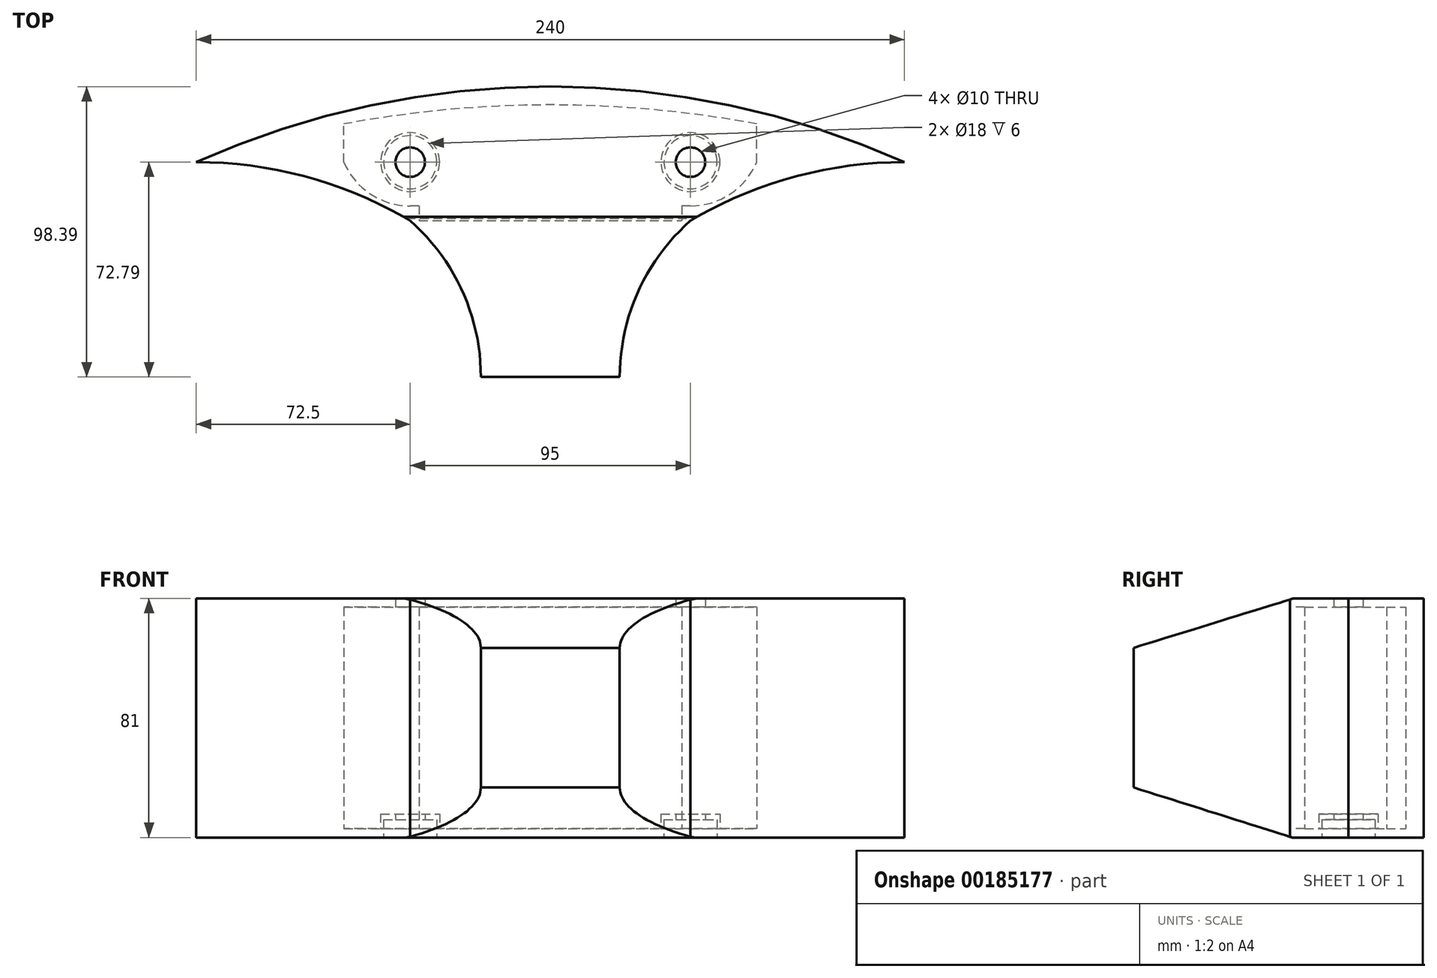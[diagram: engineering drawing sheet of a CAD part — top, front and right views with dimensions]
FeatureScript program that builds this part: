
annotation { "Feature Type Name" : "Feature", "Feature Type Description" : "" }
export const myFeature = defineFeature(function(context is Context, id is Id, definition is map)
    precondition{}
    {
        {
            var Q0;
            Q0=qCreatedBy(makeId("Top.planeOp"),FACE);
            var sketch = newSketch(context, id + "F0", { "sketchPlane" : qUnion([Q0])});
            skLineSegment(sketch, "E0.bottom", {"start": v(47.5, 12.5) * mm, "end": v(-47.5, 12.5) * mm, "construction": true});
            skLineSegment(sketch, "E0.top", {"start": v(47.5, -12.5) * mm, "end": v(-47.5, -12.5) * mm, "construction": true});
            skLineSegment(sketch, "E0.left", {"start": v(47.5, 12.5) * mm, "end": v(47.5, -12.5) * mm, "construction": true});
            skLineSegment(sketch, "E0.right", {"start": v(-47.5, 12.5) * mm, "end": v(-47.5, -12.5) * mm, "construction": true});
            skPoint(sketch, "E0.middle", {"position": v(0, 0) * mm});
            skCircle(sketch, "E1", {"center": v(-47.5, 0) * mm, "radius": 12.5 * mm, "construction": true});
            skCircle(sketch, "E2", {"center": v(47.5, 0) * mm, "radius": 12.5 * mm, "construction": true});
            skLineSegment(sketch, "E3", {"start": v(0, 12.5) * mm, "end": v(0, -72.5) * mm, "construction": true});
            skPoint(sketch, "E3.endSnap0", {"position": v(0, 12.5) * mm});
            skLineSegment(sketch, "E4.bottom", {"start": v(-23.5, -72.5) * mm, "end": v(23.5, -72.5) * mm, "construction": true});
            skLineSegment(sketch, "E4.top", {"start": v(-23.5, -72.5) * mm, "end": v(23.5, -72.5) * mm, "construction": true});
            skLineSegment(sketch, "E4.left", {"start": v(-23.5, -72.5) * mm, "end": v(-23.5, -72.5) * mm});
            skLineSegment(sketch, "E4.right", {"start": v(23.5, -72.5) * mm, "end": v(23.5, -72.5) * mm});
            skPoint(sketch, "E4.middle", {"position": v(0, -72.5) * mm});
            skLineSegment(sketch, "E5.bottom", {"start": v(47.5, -19.83) * mm, "end": v(-47.5, -19.83) * mm});
            skLineSegment(sketch, "E5.top", {"start": v(47.5, -14.83) * mm, "end": v(-47.5, -14.83) * mm});
            skLineSegment(sketch, "E5.left", {"start": v(47.5, -19.83) * mm, "end": v(47.5, -14.83) * mm});
            skLineSegment(sketch, "E5.right", {"start": v(-47.5, -19.83) * mm, "end": v(-47.5, -14.83) * mm});
            skPoint(sketch, "E5.middle", {"position": v(0, -17.33) * mm});
            skLineSegment(sketch, "E6.bottom", {"start": v(120, 0) * mm, "end": v(-120, 0) * mm, "construction": true});
            skLineSegment(sketch, "E6.top", {"start": v(120, 0) * mm, "end": v(-120, 0) * mm, "construction": true});
            skLineSegment(sketch, "E6.left", {"start": v(120, 0) * mm, "end": v(120, 0) * mm});
            skLineSegment(sketch, "E6.right", {"start": v(-120, 0) * mm, "end": v(-120, 0) * mm});
            skArc(sketch, "E7", {"start": v(-47.5, -19.83) * mm, "mid": v(-82.42, -5.05) * mm, "end": v(-120, 0) * mm});
            skArc(sketch, "E8", {"start": v(120, 0) * mm, "mid": v(82.42, -5.05) * mm, "end": v(47.5, -19.83) * mm});
            skArc(sketch, "E9", {"start": v(120, 0) * mm, "mid": v(0, 25.6) * mm, "end": v(-120, 0) * mm});
            skArc(sketch, "E10", {"start": v(-70, 0) * mm, "mid": v(-60.97, -10.79) * mm, "end": v(-47.5, -14.83) * mm});
            skArc(sketch, "E11", {"start": v(47.5, -14.83) * mm, "mid": v(60.97, -10.79) * mm, "end": v(70, 0) * mm});
            skArc(sketch, "E12", {"start": v(70, 12.91) * mm, "mid": v(0, 19.4) * mm, "end": v(-70, 12.91) * mm});
            skLineSegment(sketch, "E13", {"start": v(-70, 0) * mm, "end": v(-70, 12.91) * mm});
            skLineSegment(sketch, "E14", {"start": v(70, 0) * mm, "end": v(70, 12.91) * mm});
            skSolve(sketch);
        }
        {
            var Q0;
            Q0=qSketchRegion(id+"F0",true);
            extrude(context, id + "F1", {"entities" : qUnion([Q0]), "depth" : 75 * mm});
        }
        {
            var Q0;
            Q0=makeQuery(id+"F1.opExtrude","CAP_FACE",FACE,{"disambiguationData":[OSD([sQuery(id+"F0.wireOp",EDGE,"E5.bottom"),sQuery(id+"F0.wireOp",EDGE,"E5.top"),sQuery(id+"F0.wireOp",EDGE,"E7"),sQuery(id+"F0.wireOp",EDGE,"E8"),sQuery(id+"F0.wireOp",EDGE,"E9"),sQuery(id+"F0.wireOp",EDGE,"E10"),sQuery(id+"F0.wireOp",EDGE,"E11"),sQuery(id+"F0.wireOp",EDGE,"E12"),sQuery(id+"F0.wireOp",EDGE,"E13"),sQuery(id+"F0.wireOp",EDGE,"E14")])],"isStart":true});
            var sketch = newSketch(context, id + "F2", { "sketchPlane" : qUnion([Q0])});
            skArc(sketch, "E15", {"start": v(-120, 0) * mm, "mid": v(-82.42, 5.05) * mm, "end": v(-47.5, 19.83) * mm});
            skArc(sketch, "E16", {"start": v(47.5, 19.83) * mm, "mid": v(82.42, 5.05) * mm, "end": v(120, 0) * mm});
            skArc(sketch, "E17", {"start": v(-120, 0) * mm, "mid": v(0, -25.6) * mm, "end": v(120, 0) * mm});
            skLineSegment(sketch, "E18", {"start": v(-47.5, 19.83) * mm, "end": v(47.5, 19.83) * mm});
            skSolve(sketch);
        }
        {
            var Q0;
            Q0=qSketchRegion(id+"F2",true);
            extrude(context, id + "F3", {"entities" : qUnion([Q0]), "operationType" : NewBodyOperationType.ADD, "depth" : 3 * mm});
        }
        {
            var Q0;
            Q0=makeQuery(id+"F3.opExtrude","CAP_FACE",FACE,{"disambiguationData":[OSD([sQuery(id+"F2.wireOp",EDGE,"E15"),sQuery(id+"F2.wireOp",EDGE,"E16"),sQuery(id+"F2.wireOp",EDGE,"E17"),sQuery(id+"F2.wireOp",EDGE,"E18")])],"isStart":false});
            var sketch = newSketch(context, id + "F4", { "sketchPlane" : qUnion([Q0])});
            skLineSegment(sketch, "E19.bottom", {"start": v(47.5, 12.5) * mm, "end": v(-47.5, 12.5) * mm, "construction": true});
            skLineSegment(sketch, "E19.top", {"start": v(47.5, -12.5) * mm, "end": v(-47.5, -12.5) * mm, "construction": true});
            skLineSegment(sketch, "E19.left", {"start": v(47.5, 12.5) * mm, "end": v(47.5, -12.5) * mm, "construction": true});
            skLineSegment(sketch, "E19.right", {"start": v(-47.5, 12.5) * mm, "end": v(-47.5, -12.5) * mm, "construction": true});
            skPoint(sketch, "E19.middle", {"position": v(0, 0) * mm});
            skCircle(sketch, "E20", {"center": v(-47.5, 0) * mm, "radius": 10 * mm});
            skCircle(sketch, "E21", {"center": v(47.5, 0) * mm, "radius": 10 * mm});
            skSolve(sketch);
        }
        {
            var Q0;
            Q0=qSketchRegion(id+"F4",true);
            extrude(context, id + "F5", {"entities" : qUnion([Q0]), "operationType" : NewBodyOperationType.ADD, "oppositeDirection" : true, "depth" : 8 * mm});
        }
        {
            var Q0;
            Q0=makeQuery(id+"F3.opExtrude","CAP_FACE",FACE,{"disambiguationData":[OSD([sQuery(id+"F2.wireOp",EDGE,"E15"),sQuery(id+"F2.wireOp",EDGE,"E16"),sQuery(id+"F2.wireOp",EDGE,"E17"),sQuery(id+"F2.wireOp",EDGE,"E18")])],"isStart":false});
            var sketch = newSketch(context, id + "F6", { "sketchPlane" : qUnion([Q0])});
            skCircle(sketch, "E22", {"center": v(-47.5, 0) * mm, "radius": 9 * mm});
            skCircle(sketch, "E23", {"center": v(47.5, 0) * mm, "radius": 9 * mm});
            skSolve(sketch);
        }
        {
            var Q0;
            Q0=qSketchRegion(id+"F6",true);
            extrude(context, id + "F7", {"entities" : qUnion([Q0]), "operationType" : NewBodyOperationType.REMOVE, "oppositeDirection" : true, "depth" : 6 * mm});
        }
        {
            var Q0;
            Q0=makeQuery(id+"F3.opExtrude","CAP_FACE",FACE,{"disambiguationData":[OSD([sQuery(id+"F2.wireOp",EDGE,"E15"),sQuery(id+"F2.wireOp",EDGE,"E16"),sQuery(id+"F2.wireOp",EDGE,"E17"),sQuery(id+"F2.wireOp",EDGE,"E18")])],"isStart":false});
            var sketch = newSketch(context, id + "F8", { "sketchPlane" : qUnion([Q0])});
            skCircle(sketch, "E24", {"center": v(-47.5, 0) * mm, "radius": 5 * mm});
            skCircle(sketch, "E25", {"center": v(47.5, 0) * mm, "radius": 5 * mm});
            skSolve(sketch);
        }
        {
            var Q0;
            Q0=qSketchRegion(id+"F8",true);
            extrude(context, id + "F9", {"entities" : qUnion([Q0]), "operationType" : NewBodyOperationType.REMOVE, "oppositeDirection" : true, "depth" : 25 * mm});
        }
        {
            var Q0;
            Q0=makeQuery(id+"F1.opExtrude","CAP_FACE",FACE,{"disambiguationData":[OSD([sQuery(id+"F0.wireOp",EDGE,"E5.bottom"),sQuery(id+"F0.wireOp",EDGE,"E5.top"),sQuery(id+"F0.wireOp",EDGE,"E7"),sQuery(id+"F0.wireOp",EDGE,"E8"),sQuery(id+"F0.wireOp",EDGE,"E9"),sQuery(id+"F0.wireOp",EDGE,"E10"),sQuery(id+"F0.wireOp",EDGE,"E11"),sQuery(id+"F0.wireOp",EDGE,"E12"),sQuery(id+"F0.wireOp",EDGE,"E13"),sQuery(id+"F0.wireOp",EDGE,"E14")])],"isStart":false});
            var sketch = newSketch(context, id + "F10", { "sketchPlane" : qUnion([Q0])});
            skArc(sketch, "E26", {"start": v(120, 0) * mm, "mid": v(0, 25.6) * mm, "end": v(-120, 0) * mm});
            skArc(sketch, "E27", {"start": v(-47.5, -19.83) * mm, "mid": v(-82.42, -5.05) * mm, "end": v(-120, 0) * mm});
            skArc(sketch, "E28", {"start": v(120, 0) * mm, "mid": v(82.42, -5.05) * mm, "end": v(47.5, -19.83) * mm});
            skLineSegment(sketch, "E29", {"start": v(-47.5, -19.83) * mm, "end": v(47.5, -19.83) * mm});
            skCircle(sketch, "E30", {"center": v(-47.5, 0) * mm, "radius": 5 * mm});
            skCircle(sketch, "E31", {"center": v(47.5, 0) * mm, "radius": 5 * mm});
            skSolve(sketch);
        }
        {
            var Q0;
            Q0=qSketchRegion(id+"F10",true);
            extrude(context, id + "F11", {"entities" : qUnion([Q0]), "operationType" : NewBodyOperationType.ADD, "depth" : 3 * mm});
        }
        {
            var Q0;
            Q0=makeQuery(id+"F11.boolean.opBoolean","MERGE",FACE,{"derivedFrom":[makeQuery(id+"F3.boolean.opBoolean","MERGE",FACE,{"derivedFrom":[makeQuery(id+"F1.opExtrude","SWEPT_FACE",FACE,{"disambiguationData":[OSD([sQuery(id+"F0.wireOp",EDGE,"E5.bottom")])]}),makeQuery(id+"F3.opExtrude","SWEPT_FACE",FACE,{"disambiguationData":[OSD([sQuery(id+"F2.wireOp",EDGE,"E18")])]})]}),makeQuery(id+"F11.opExtrude","SWEPT_FACE",FACE,{"disambiguationData":[OSD([sQuery(id+"F10.wireOp",EDGE,"E29")])]})]});
            var sketch = newSketch(context, id + "F12", { "sketchPlane" : qUnion([Q0])});
            skLineSegment(sketch, "E32.bottom", {"start": v(-47.5, 78) * mm, "end": v(47.5, 78) * mm});
            skLineSegment(sketch, "E32.top", {"start": v(-47.5, -3) * mm, "end": v(47.5, -3) * mm});
            skLineSegment(sketch, "E32.left", {"start": v(-47.5, 78) * mm, "end": v(-47.5, -3) * mm});
            skLineSegment(sketch, "E32.right", {"start": v(47.5, 78) * mm, "end": v(47.5, -3) * mm});
            skSolve(sketch);
        }
        {
            var Q0;
            {var subQ3=sQuery(id+"F12.wireOp",EDGE,"E32.bottom");Q0=makeQuery(id+"F12.imprint","IMPRINT",FACE,{"disambiguationData":[TD([[makeQuery(id+"F12.imprint","IMPRINT",EDGE,{"derivedFrom":subQ3}),1.0]])]});}
            var sketch = newSketch(context, id + "F13", { "sketchPlane" : qUnion([Q0])});
            skLineSegment(sketch, "E33.bottom", {"start": v(-44.5, 75) * mm, "end": v(44.5, 75) * mm});
            skLineSegment(sketch, "E33.top", {"start": v(-44.5, 0) * mm, "end": v(44.5, 0) * mm});
            skLineSegment(sketch, "E33.left", {"start": v(-44.5, 75) * mm, "end": v(-44.5, 0) * mm});
            skLineSegment(sketch, "E33.right", {"start": v(44.5, 75) * mm, "end": v(44.5, 0) * mm});
            skSolve(sketch);
        }
        {
            var Q0;
            Q0=qSketchRegion(id+"F13",true);
            extrude(context, id + "F14", {"entities" : qUnion([Q0]), "operationType" : NewBodyOperationType.REMOVE, "oppositeDirection" : true, "depth" : 5 * mm});
        }
        {
            var Q0;
            Q0=qCreatedBy(makeId("Front.planeOp"),FACE);
            cPlane(context, id + "F15", {"entities" : qUnion([Q0]), "cplaneType" : CPlaneType.OFFSET, "offset" : 72.5 * mm, "width" : 150 * mm, "height" : 150 * mm});
        }
        {
            var Q0;
            Q0=qCreatedBy(id+"F15.planeOp",FACE);
            var sketch = newSketch(context, id + "F16", { "sketchPlane" : qUnion([Q0])});
            skCircle(sketch, "E34", {"center": v(0, 37.5) * mm, "radius": 23.5 * mm});
            skSolve(sketch);
        }
        {
            var Q0;
            Q0=makeQuery(id+"F11.opExtrude","CAP_FACE",FACE,{"disambiguationData":[OSD([sQuery(id+"F10.wireOp",EDGE,"E26"),sQuery(id+"F10.wireOp",EDGE,"E27"),sQuery(id+"F10.wireOp",EDGE,"E28"),sQuery(id+"F10.wireOp",EDGE,"E29"),sQuery(id+"F10.wireOp",EDGE,"E30"),sQuery(id+"F10.wireOp",EDGE,"E31")])],"isStart":false});
            var sketch = newSketch(context, id + "F17", { "sketchPlane" : qUnion([Q0])});
            skLineSegment(sketch, "E35.bottom", {"start": v(-23.5, -72.79) * mm, "end": v(23.5, -72.79) * mm});
            skLineSegment(sketch, "E35.top", {"start": v(-23.5, -72.58) * mm, "end": v(23.5, -72.58) * mm});
            skLineSegment(sketch, "E35.left", {"start": v(-23.5, -72.79) * mm, "end": v(-23.5, -72.58) * mm});
            skLineSegment(sketch, "E35.right", {"start": v(23.5, -72.79) * mm, "end": v(23.5, -72.58) * mm});
            skPoint(sketch, "E35.middle", {"position": v(0, -72.68) * mm});
            skArc(sketch, "E36", {"start": v(-23.5, -72.79) * mm, "mid": v(-29.78, -43.71) * mm, "end": v(-47.5, -19.83) * mm});
            skArc(sketch, "E37", {"start": v(47.5, -19.83) * mm, "mid": v(29.78, -43.71) * mm, "end": v(23.5, -72.79) * mm});
            skLineSegment(sketch, "E38", {"start": v(-47.5, -19.83) * mm, "end": v(47.5, -19.83) * mm});
            skSolve(sketch);
        }
        {
            var Q0;
            Q0 = qSketchRegion(id + "F17", true);
            extrude(context, id + "F18", {"entities" : qUnion([Q0]), "operationType" : NewBodyOperationType.ADD, "oppositeDirection" : true, "depth" : 81 * mm});
        }
        {
            var Q0;
            Q0=qCreatedBy(makeId("Right.planeOp"),FACE);
            var sketch = newSketch(context, id + "F19", { "sketchPlane" : qUnion([Q0])});
            skLineSegment(sketch, "E39", {"start": v(-15, 79.1) * mm, "end": v(-70.5, 61.97) * mm});
            skLineSegment(sketch, "E40", {"start": v(-70.5, 61.97) * mm, "end": v(-73.13, 61.15) * mm});
            skLineSegment(sketch, "E41", {"start": v(-73.13, 61.15) * mm, "end": v(-73.13, 79.1) * mm});
            skLineSegment(sketch, "E42", {"start": v(-73.13, 79.1) * mm, "end": v(-15, 79.1) * mm});
            skSolve(sketch);
        }
        {
            var Q0;
            Q0 = qSketchRegion(id + "F19", true);
            extrude(context, id + "F20", {"entities" : qUnion([Q0]), "operationType" : NewBodyOperationType.REMOVE, "endBound" : BoundingType.SYMMETRIC, "oppositeDirection" : true, "depth" : 100 * mm});
        }
        {
            var Q0;
            Q0=qCreatedBy(makeId("Right.planeOp"),FACE);
            var sketch = newSketch(context, id + "F21", { "sketchPlane" : qUnion([Q0])});
            skLineSegment(sketch, "E43", {"start": v(-18.87, -3.06) * mm, "end": v(-74.2, 14.37) * mm});
            skLineSegment(sketch, "E44", {"start": v(-74.2, 14.37) * mm, "end": v(-74.2, -9.58) * mm});
            skLineSegment(sketch, "E45", {"start": v(-74.2, -9.58) * mm, "end": v(-18.87, -3.24) * mm});
            skLineSegment(sketch, "E46", {"start": v(-18.87, -3.06) * mm, "end": v(-18.87, -3.24) * mm});
            skSolve(sketch);
        }
        {
            var Q0;
            Q0 = qSketchRegion(id + "F21", true);
            extrude(context, id + "F22", {"entities" : qUnion([Q0]), "operationType" : NewBodyOperationType.REMOVE, "endBound" : BoundingType.SYMMETRIC, "oppositeDirection" : true, "depth" : 100 * mm});
        }
    });
